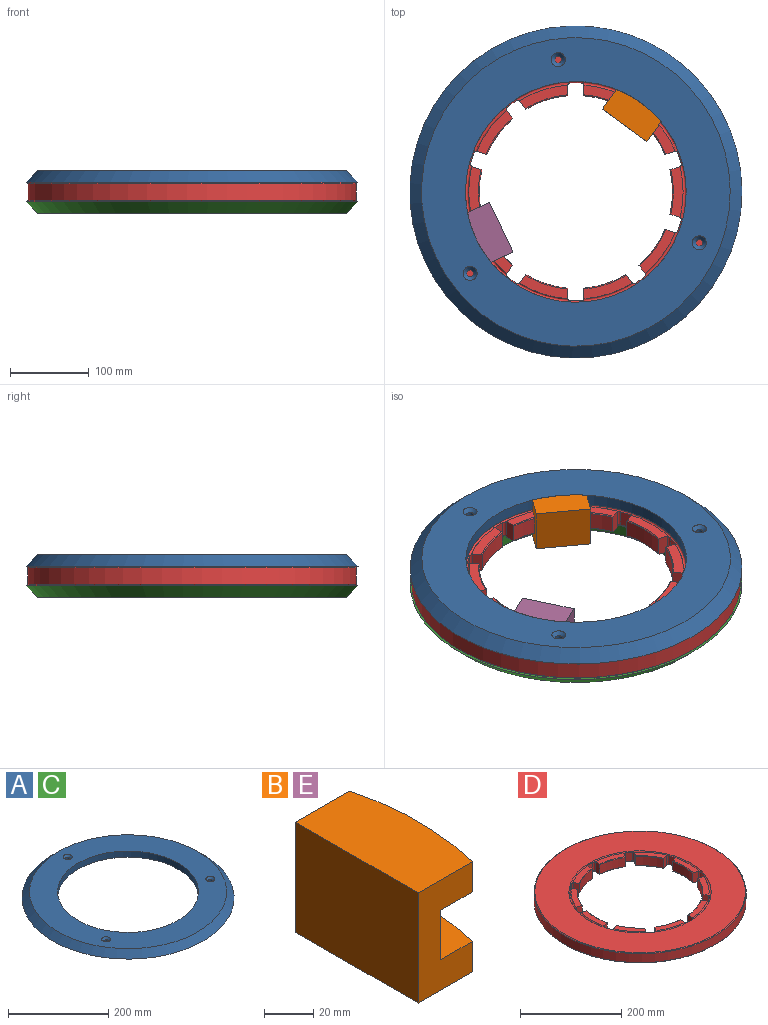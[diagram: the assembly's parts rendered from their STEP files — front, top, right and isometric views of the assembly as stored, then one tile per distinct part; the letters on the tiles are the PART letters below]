
ASSEMBLY  parts=5 mates=4
PART A: 10 faces, bbox 423x423x15 mm
  f0: cylinder r=140.5mm len=281mm, axis (0,0,-1), area 13241.8mm2, adj f1,f2
  f1: plane 393x393mm, normal (0,0,1), area 58531.5mm2, adj f0,f3,f5,f7,f9
  f2: plane 423x423mm, normal (0,0,-1), area 78323.8mm2, adj f0,f3,f4,f6,f8
  f3: cone r=196.5mm half-angle=45deg, axis (0,0,-1), area 27190.4mm2, adj f1,f2
  f4: cylinder r=4.5mm len=10.54mm, axis (0,0,1), area 298mm2, adj f2,f5
  f5: cone r=4.5mm half-angle=45deg, axis (0,0,1), area 266.7mm2, adj f1,f4
  f6: cylinder r=4.5mm len=10.54mm, axis (0,0,1), area 298mm2, adj f2,f7
  f7: cone r=4.5mm half-angle=45deg, axis (0,0,1), area 266.7mm2, adj f1,f6
  f8: cylinder r=4.5mm len=10.54mm, axis (0,0,1), area 298mm2, adj f2,f9
  f9: cone r=4.5mm half-angle=45deg, axis (0,0,1), area 266.7mm2, adj f1,f8
PART B: 16 faces, bbox 35.4x70x54.5 mm
  f0: plane 70x22.58mm, normal (0,0,-1), area 917.1mm2, adj f3,f4,f6,f8,f9,f10,f11,f12
  f1: cylinder r=140.5mm len=70mm, axis (0,0,1), area 1061.2mm2, adj f2,f7,f13,f14
  f2: plane 70x22.58mm, normal (0,0,1), area 917.1mm2, adj f1,f3,f6,f8,f9,f10,f11,f12
  f3: cylinder r=123mm len=24.75mm, axis (0,0,1), area 618.1mm2, adj f0,f2,f8,f13
  f4: cylinder r=140.5mm len=70mm, axis (0,0,1), area 1061.2mm2, adj f0,f5,f13,f14
  f5: plane 70x35.35mm, normal (0,0,1), area 2372mm2, adj f4,f13,f14,f15
  f6: cylinder r=123mm len=24.75mm, axis (0,0,1), area 618.1mm2, adj f0,f2,f9,f14
  f7: plane 70x35.35mm, normal (0,0,-1), area 2372mm2, adj f1,f13,f14,f15
  f8: plane 24.5x13.07mm, normal (0,1,0), area 320.2mm2, adj f0,f2,f3,f11
  f9: plane 24.5x13.07mm, normal (0,-1,0), area 320.2mm2, adj f0,f2,f6,f10
  f10: cylinder r=3.17mm len=24.5mm, axis (0,0,-1), area 122.2mm2, adj f0,f2,f9,f12
  f11: cylinder r=3.17mm len=24.5mm, axis (0,0,-1), area 122.2mm2, adj f0,f2,f8,f12
  f12: plane 24.5x14.15mm, normal (1,0,0), area 346.7mm2, adj f0,f2,f10,f11
  f13: plane 54.5x30.92mm, normal (0,1,0), area 1240.5mm2, adj f0,f1,f2,f3,f4,f5,f7,f15
  f14: plane 54.5x30.92mm, normal (0,-1,0), area 1240.5mm2, adj f0,f1,f2,f4,f5,f6,f7,f15
  f15: plane 70x54.5mm, normal (-1,0,0), area 3815mm2, adj f5,f7,f13,f14
PART C: same geometry as A
PART D: 107 faces, bbox 419x419x27.3 mm
  f0: plane 56.14x45.29mm, normal (0,0,1), area 758.3mm2, adj f7,f9,f11,f16,f18,f95
  f1: cone r=123mm half-angle=45deg, axis (0,0,1), area 92.3mm2, adj f8,f90,f96,f101
  f2: cylinder r=123mm len=45.51mm, axis (0,0,-1), area 1260.9mm2, adj f9,f11,f13,f18
  f3: cone r=124.14mm half-angle=45deg, axis (0,0,-1), area 92.3mm2, adj f4,f8,f90,f101
  f4: plane 61.53x30mm, normal (0,0,-1), area 758.3mm2, adj f3,f6,f8,f94,f101,f102
  f5: plane 20.63x11.45mm, normal (-0.59,-0.81,0), area 291.1mm2, adj f6,f7,f94,f95
  f6: cylinder r=3.17mm len=24.5mm, axis (0,0,1), area 106.2mm2, adj f4,f5,f8,f94,f95,f96
  f7: cylinder r=3.17mm len=24.5mm, axis (0,0,1), area 106.2mm2, adj f0,f5,f9,f14,f94,f95
  f8: plane 24.5x10.57mm, normal (0.81,-0.59,0), area 318.9mm2, adj f1,f3,f4,f6,f90,f96
  f9: plane 24.5x10.57mm, normal (-0.81,0.59,0), area 318.9mm2, adj f0,f2,f7,f11,f13,f14
  f10: plane 64.7x15.67mm, normal (0,0,1), area 758.3mm2, adj f17,f19,f21,f26,f28,f95
  f11: cone r=123mm half-angle=45deg, axis (0,0,1), area 92.3mm2, adj f0,f2,f9,f18
  f12: cylinder r=123mm len=56.26mm, axis (0,0,-1), area 1260.9mm2, adj f19,f21,f23,f28
  f13: cone r=124.14mm half-angle=45deg, axis (0,0,-1), area 92.3mm2, adj f2,f9,f14,f18
  f14: plane 56.14x45.29mm, normal (0,0,-1), area 758.3mm2, adj f7,f9,f13,f16,f18,f94
  f15: plane 20.63x13.46mm, normal (-0.95,-0.31,0), area 291.1mm2, adj f16,f17,f94,f95
  f16: cylinder r=3.17mm len=24.5mm, axis (0,0,1), area 106.2mm2, adj f0,f14,f15,f18,f94,f95
  f17: cylinder r=3.17mm len=24.5mm, axis (0,0,1), area 106.2mm2, adj f10,f15,f19,f24,f94,f95
  f18: plane 24.5x12.43mm, normal (0.31,-0.95,0), area 318.9mm2, adj f0,f2,f11,f13,f14,f16
  f19: plane 24.5x12.43mm, normal (-0.31,0.95,0), area 318.9mm2, adj f10,f12,f17,f21,f23,f24
  f20: plane 56.14x45.29mm, normal (0,0,1), area 758.3mm2, adj f27,f29,f31,f36,f38,f95
  f21: cone r=123mm half-angle=45deg, axis (0,0,1), area 92.3mm2, adj f10,f12,f19,f28
  f22: cylinder r=123mm len=45.51mm, axis (0,0,-1), area 1260.9mm2, adj f29,f31,f33,f38
  f23: cone r=124.14mm half-angle=45deg, axis (0,0,-1), area 92.3mm2, adj f12,f19,f24,f28
  f24: plane 64.7x15.67mm, normal (0,0,-1), area 758.3mm2, adj f17,f19,f23,f26,f28,f94
  f25: plane 20.63x13.46mm, normal (-0.95,0.31,0), area 291.1mm2, adj f26,f27,f94,f95
  f26: cylinder r=3.17mm len=24.5mm, axis (0,0,1), area 106.2mm2, adj f10,f24,f25,f28,f94,f95
  f27: cylinder r=3.17mm len=24.5mm, axis (0,0,1), area 106.2mm2, adj f20,f25,f29,f34,f94,f95
  f28: plane 24.5x12.43mm, normal (-0.31,-0.95,0), area 318.9mm2, adj f10,f12,f21,f23,f24,f26
  f29: plane 24.5x12.43mm, normal (0.31,0.95,0), area 318.9mm2, adj f20,f22,f27,f31,f33,f34
  f30: plane 61.53x30mm, normal (0,0,1), area 758.3mm2, adj f37,f39,f41,f46,f48,f95
  f31: cone r=123mm half-angle=45deg, axis (0,0,1), area 92.3mm2, adj f20,f22,f29,f38
  f32: cylinder r=123mm len=53.5mm, axis (0,0,-1), area 1260.9mm2, adj f39,f41,f43,f48
  f33: cone r=124.14mm half-angle=45deg, axis (0,0,-1), area 92.3mm2, adj f22,f29,f34,f38
  f34: plane 56.14x45.29mm, normal (0,0,-1), area 758.3mm2, adj f27,f29,f33,f36,f38,f94
  f35: plane 20.63x11.45mm, normal (-0.59,0.81,0), area 291.1mm2, adj f36,f37,f94,f95
  f36: cylinder r=3.17mm len=24.5mm, axis (0,0,1), area 106.2mm2, adj f20,f34,f35,f38,f94,f95
  f37: cylinder r=3.17mm len=24.5mm, axis (0,0,1), area 106.2mm2, adj f30,f35,f39,f44,f94,f95
  f38: plane 24.5x10.57mm, normal (-0.81,-0.59,0), area 318.9mm2, adj f20,f22,f31,f33,f34,f36
  f39: plane 24.5x10.57mm, normal (0.81,0.59,0), area 318.9mm2, adj f30,f32,f37,f41,f43,f44
  f40: plane 61.53x30mm, normal (0,0,1), area 758.3mm2, adj f47,f49,f51,f56,f58,f95
  f41: cone r=123mm half-angle=45deg, axis (0,0,1), area 92.3mm2, adj f30,f32,f39,f48
  f42: cylinder r=123mm len=53.5mm, axis (0,0,-1), area 1260.9mm2, adj f49,f51,f53,f58
  f43: cone r=124.14mm half-angle=45deg, axis (0,0,-1), area 92.3mm2, adj f32,f39,f44,f48
  f44: plane 61.53x30mm, normal (0,0,-1), area 758.3mm2, adj f37,f39,f43,f46,f48,f94
  f45: plane 20.63x14.15mm, normal (0,1,0), area 291.1mm2, adj f46,f47,f94,f95
  f46: cylinder r=3.17mm len=24.5mm, axis (0,0,1), area 106.2mm2, adj f30,f44,f45,f48,f94,f95
  f47: cylinder r=3.17mm len=24.5mm, axis (0,0,1), area 106.2mm2, adj f40,f45,f49,f54,f94,f95
  f48: plane 24.5x13.07mm, normal (-1,0,0), area 318.9mm2, adj f30,f32,f41,f43,f44,f46
  f49: plane 24.5x13.07mm, normal (1,0,0), area 318.9mm2, adj f40,f42,f47,f51,f53,f54
  f50: plane 56.14x45.29mm, normal (0,0,1), area 758.3mm2, adj f57,f59,f61,f66,f68,f95
  f51: cone r=123mm half-angle=45deg, axis (0,0,1), area 92.3mm2, adj f40,f42,f49,f58
  f52: cylinder r=123mm len=45.51mm, axis (0,0,-1), area 1260.9mm2, adj f59,f61,f63,f68
  f53: cone r=124.14mm half-angle=45deg, axis (0,0,-1), area 92.3mm2, adj f42,f49,f54,f58
  f54: plane 61.53x30mm, normal (0,0,-1), area 758.3mm2, adj f47,f49,f53,f56,f58,f94
  f55: plane 20.63x11.45mm, normal (0.59,0.81,0), area 291.1mm2, adj f56,f57,f94,f95
  f56: cylinder r=3.17mm len=24.5mm, axis (0,0,1), area 106.2mm2, adj f40,f54,f55,f58,f94,f95
  f57: cylinder r=3.17mm len=24.5mm, axis (0,0,1), area 106.2mm2, adj f50,f55,f59,f64,f94,f95
  f58: plane 24.5x10.57mm, normal (-0.81,0.59,0), area 318.9mm2, adj f40,f42,f51,f53,f54,f56
  f59: plane 24.5x10.57mm, normal (0.81,-0.59,0), area 318.9mm2, adj f50,f52,f57,f61,f63,f64
  f60: plane 64.7x15.67mm, normal (0,0,1), area 758.3mm2, adj f67,f69,f71,f76,f78,f95
  f61: cone r=123mm half-angle=45deg, axis (0,0,1), area 92.3mm2, adj f50,f52,f59,f68
  f62: cylinder r=123mm len=56.26mm, axis (0,0,-1), area 1260.9mm2, adj f69,f71,f73,f78
  f63: cone r=124.14mm half-angle=45deg, axis (0,0,-1), area 92.3mm2, adj f52,f59,f64,f68
  f64: plane 56.14x45.29mm, normal (0,0,-1), area 758.3mm2, adj f57,f59,f63,f66,f68,f94
  f65: plane 20.63x13.46mm, normal (0.95,0.31,0), area 291.1mm2, adj f66,f67,f94,f95
  f66: cylinder r=3.17mm len=24.5mm, axis (0,0,1), area 106.2mm2, adj f50,f64,f65,f68,f94,f95
  f67: cylinder r=3.17mm len=24.5mm, axis (0,0,1), area 106.2mm2, adj f60,f65,f69,f74,f94,f95
  f68: plane 24.5x12.43mm, normal (-0.31,0.95,0), area 318.9mm2, adj f50,f52,f61,f63,f64,f66
  f69: plane 24.5x12.43mm, normal (0.31,-0.95,0), area 318.9mm2, adj f60,f62,f67,f71,f73,f74
  f70: plane 56.14x45.29mm, normal (0,0,1), area 758.3mm2, adj f77,f79,f81,f86,f88,f95
  f71: cone r=123mm half-angle=45deg, axis (0,0,1), area 92.3mm2, adj f60,f62,f69,f78
  f72: cylinder r=123mm len=45.51mm, axis (0,0,-1), area 1260.9mm2, adj f79,f81,f83,f88
  f73: cone r=124.14mm half-angle=45deg, axis (0,0,-1), area 92.3mm2, adj f62,f69,f74,f78
  f74: plane 64.7x15.67mm, normal (0,0,-1), area 758.3mm2, adj f67,f69,f73,f76,f78,f94
  f75: plane 20.63x13.46mm, normal (0.95,-0.31,0), area 291.1mm2, adj f76,f77,f94,f95
  f76: cylinder r=3.17mm len=24.5mm, axis (0,0,1), area 106.2mm2, adj f60,f74,f75,f78,f94,f95
  f77: cylinder r=3.17mm len=24.5mm, axis (0,0,1), area 106.2mm2, adj f70,f75,f79,f84,f94,f95
  f78: plane 24.5x12.43mm, normal (0.31,0.95,0), area 318.9mm2, adj f60,f62,f71,f73,f74,f76
  f79: plane 24.5x12.43mm, normal (-0.31,-0.95,0), area 318.9mm2, adj f70,f72,f77,f81,f83,f84
  f80: plane 61.53x30mm, normal (0,0,1), area 758.3mm2, adj f87,f89,f95,f99,f100,f104
  f81: cone r=123mm half-angle=45deg, axis (0,0,1), area 92.3mm2, adj f70,f72,f79,f88
  f82: cylinder r=123mm len=53.5mm, axis (0,0,-1), area 1260.9mm2, adj f89,f100,f103,f104
  f83: cone r=124.14mm half-angle=45deg, axis (0,0,-1), area 92.3mm2, adj f72,f79,f84,f88
  f84: plane 56.14x45.29mm, normal (0,0,-1), area 758.3mm2, adj f77,f79,f83,f86,f88,f94
  f85: plane 20.63x11.45mm, normal (0.59,-0.81,0), area 291.1mm2, adj f86,f87,f94,f95
  f86: cylinder r=3.17mm len=24.5mm, axis (0,0,1), area 106.2mm2, adj f70,f84,f85,f88,f94,f95
  f87: cylinder r=3.17mm len=24.5mm, axis (0,0,1), area 106.2mm2, adj f80,f85,f89,f94,f95,f97
  f88: plane 24.5x10.57mm, normal (0.81,0.59,0), area 318.9mm2, adj f70,f72,f81,f83,f84,f86
  f89: plane 24.5x10.57mm, normal (-0.81,-0.59,0), area 318.9mm2, adj f80,f82,f87,f97,f103,f104
  f90: cylinder r=123mm len=53.5mm, axis (0,0,-1), area 1260.9mm2, adj f1,f3,f8,f101
  f91: plane 416x416mm, normal (0,0,1), area 73902mm2, adj f95,f106
  f92: plane 416x416mm, normal (0,0,-1), area 73902mm2, adj f94,f105
  f93: cylinder r=209.5mm len=419mm, axis (0,0,-1), area 28301mm2, adj f105,f106
  f94: torus R=138.5mm, axis (0,0,1), area 4776.8mm2, adj f4,f5,f6,f7,f14,f15,f16,f17
  f95: torus R=138.5mm, axis (0,0,1), area 4778.4mm2, adj f0,f5,f6,f7,f10,f15,f16,f17
  f96: plane 61.53x30mm, normal (0,0,1), area 758.3mm2, adj f1,f6,f8,f95,f101,f102
  f97: plane 61.53x30mm, normal (0,0,-1), area 758.3mm2, adj f87,f89,f94,f99,f100,f103
  f98: plane 20.63x14.15mm, normal (0,-1,0), area 291.1mm2, adj f94,f95,f99,f102
  f99: cylinder r=3.17mm len=24.5mm, axis (0,0,1), area 106.2mm2, adj f80,f94,f95,f97,f98,f100
  f100: plane 24.5x13.07mm, normal (1,0,0), area 318.9mm2, adj f80,f82,f97,f99,f103,f104
  f101: plane 24.5x13.07mm, normal (-1,0,0), area 318.9mm2, adj f1,f3,f4,f90,f96,f102
  f102: cylinder r=3.17mm len=24.5mm, axis (0,0,1), area 106.2mm2, adj f4,f94,f95,f96,f98,f101
  f103: cone r=124.14mm half-angle=45deg, axis (0,0,-1), area 92.3mm2, adj f82,f89,f97,f100
  f104: cone r=123mm half-angle=45deg, axis (0,0,1), area 92.3mm2, adj f80,f82,f89,f100
  f105: cone r=209.5mm half-angle=45deg, axis (0,0,1), area 2782.4mm2, adj f92,f93
  f106: cone r=208mm half-angle=45deg, axis (0,0,-1), area 2782.4mm2, adj f91,f93
PART E: same geometry as B
PLACE A rot(axis=(0,0,-1),112.4deg) t=(0,0,12.25)mm
PLACE B rot(axis=(-0.89,-0.45,0),180deg) t=(65.18,89.23,27.25)mm
PLACE C rot(axis=(0.1,-1,0),180deg) t=(0,0,-12.25)mm
PLACE D t=(0,0,-12.25)mm
PLACE E rot(axis=(0,0,-1),154.7deg) t=(-99.91,-47.21,-27.25)mm
MATE revolute A.f3 <-> D.f93  axis (0,0,-1) through (0,0,12.25)mm
MATE revolute C.f3 <-> D.f93  axis (0,0,1) through (0,0,-12.25)mm
MATE revolute E.f1 <-> A.f0  axis (0,0,1) through (0,0,19.75)mm
MATE revolute B.f1 <-> C.f0  axis (0,0,-1) through (0,0,-19.75)mm
